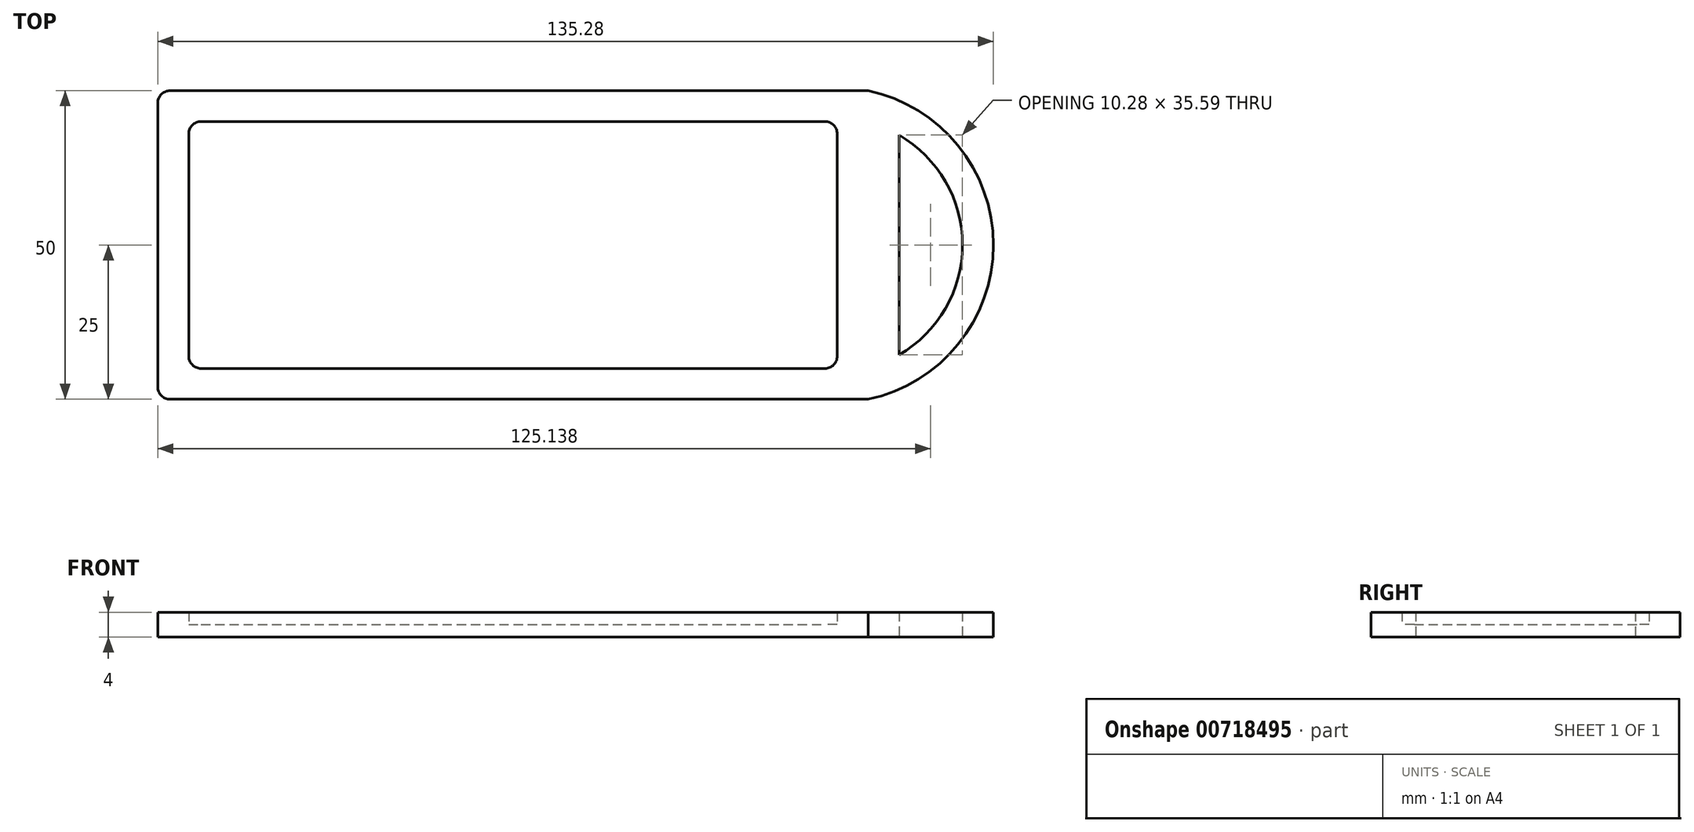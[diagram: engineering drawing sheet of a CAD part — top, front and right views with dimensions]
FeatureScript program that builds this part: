
annotation { "Feature Type Name" : "Feature", "Feature Type Description" : "" }
export const myFeature = defineFeature(function(context is Context, id is Id, definition is map)
    precondition{}
    {
        {
            var Q0;
            Q0=qCreatedBy(makeId("Top.planeOp"),FACE);
            var sketch = newSketch(context, id + "F0", { "sketchPlane" : qUnion([Q0])});
            skLineSegment(sketch, "E0.bottom", {"start": v(2, 0) * mm, "end": v(115, 0) * mm});
            skLineSegment(sketch, "E0.top", {"start": v(2, 50) * mm, "end": v(115, 50) * mm});
            skLineSegment(sketch, "E0.left", {"start": v(0, 2) * mm, "end": v(0, 48) * mm});
            skLineSegment(sketch, "E0.right", {"start": v(115, 0) * mm, "end": v(115, 50) * mm});
            skArc(sketch, "E1", {"start": v(115, 0) * mm, "mid": v(135.28, 25) * mm, "end": v(115, 50) * mm});
            skLineSegment(sketch, "E2.0", {"start": v(5, 7) * mm, "end": v(5, 43) * mm});
            skLineSegment(sketch, "E2.1", {"start": v(7, 5) * mm, "end": v(108, 5) * mm});
            skLineSegment(sketch, "E2.2", {"start": v(110, 7) * mm, "end": v(110, 43) * mm});
            skLineSegment(sketch, "E2.3", {"start": v(7, 45) * mm, "end": v(108, 45) * mm});
            skPoint(sketch, "E3.visualSharp", {"position": v(5, 45) * mm});
            skArc(sketch, "E3.filletArc", {"start": v(7, 45) * mm, "mid": v(5.59, 44.41) * mm, "end": v(5, 43) * mm});
            skPoint(sketch, "E4.visualSharp", {"position": v(5, 5) * mm});
            skArc(sketch, "E4.filletArc", {"start": v(5, 7) * mm, "mid": v(5.59, 5.59) * mm, "end": v(7, 5) * mm});
            skPoint(sketch, "E5.visualSharp", {"position": v(110, 5) * mm});
            skArc(sketch, "E5.filletArc", {"start": v(108, 5) * mm, "mid": v(109.41, 5.59) * mm, "end": v(110, 7) * mm});
            skPoint(sketch, "E6.visualSharp", {"position": v(110, 45) * mm});
            skArc(sketch, "E6.filletArc", {"start": v(110, 43) * mm, "mid": v(109.41, 44.41) * mm, "end": v(108, 45) * mm});
            skPoint(sketch, "E7.visualSharp", {"position": v(0, 50) * mm});
            skArc(sketch, "E7.filletArc", {"start": v(2, 50) * mm, "mid": v(0.59, 49.41) * mm, "end": v(0, 48) * mm});
            skPoint(sketch, "E8.visualSharp", {"position": v(0, 0) * mm});
            skArc(sketch, "E8.filletArc", {"start": v(0, 2) * mm, "mid": v(0.59, 0.59) * mm, "end": v(2, 0) * mm});
            skArc(sketch, "E9.0", {"start": v(120, 7.2) * mm, "mid": v(130.28, 25) * mm, "end": v(120, 42.8) * mm});
            skLineSegment(sketch, "E9.1", {"start": v(120, 7.2) * mm, "end": v(120, 42.8) * mm});
            skSolve(sketch);
        }
        {
            var Q0;
            Q0=makeQuery(id+"F0.imprint","IMPRINT",FACE,{"disambiguationData":[TD([[makeQuery(id+"F0.imprint","IMPRINT",EDGE,{"derivedFrom":sQuery(id+"F0.wireOp",EDGE,"E2.0")}),-1.0]])]});
            extrude(context, id + "F1", {"entities" : qUnion([Q0]), "depth" : 2 * mm, "offsetDistance" : 25 * mm});
        }
        {
            var Q0;
            Q0=makeQuery(id+"F0.imprint","IMPRINT",FACE,{"disambiguationData":[TD([[makeQuery(id+"F0.imprint","IMPRINT",EDGE,{"derivedFrom":sQuery(id+"F0.wireOp",EDGE,"E0.bottom")}),1.0]])]});
            var Q1;
            Q1=makeQuery(id+"F0.imprint","IMPRINT",FACE,{"disambiguationData":[TD([[makeQuery(id+"F0.imprint","IMPRINT",EDGE,{"derivedFrom":sQuery(id+"F0.wireOp",EDGE,"E0.right")}),-1.0]])]});
            extrude(context, id + "F2", {"entities" : qUnion([Q0, Q1]), "operationType" : NewBodyOperationType.ADD, "depth" : 4 * mm, "offsetDistance" : 25 * mm});
        }
    });
